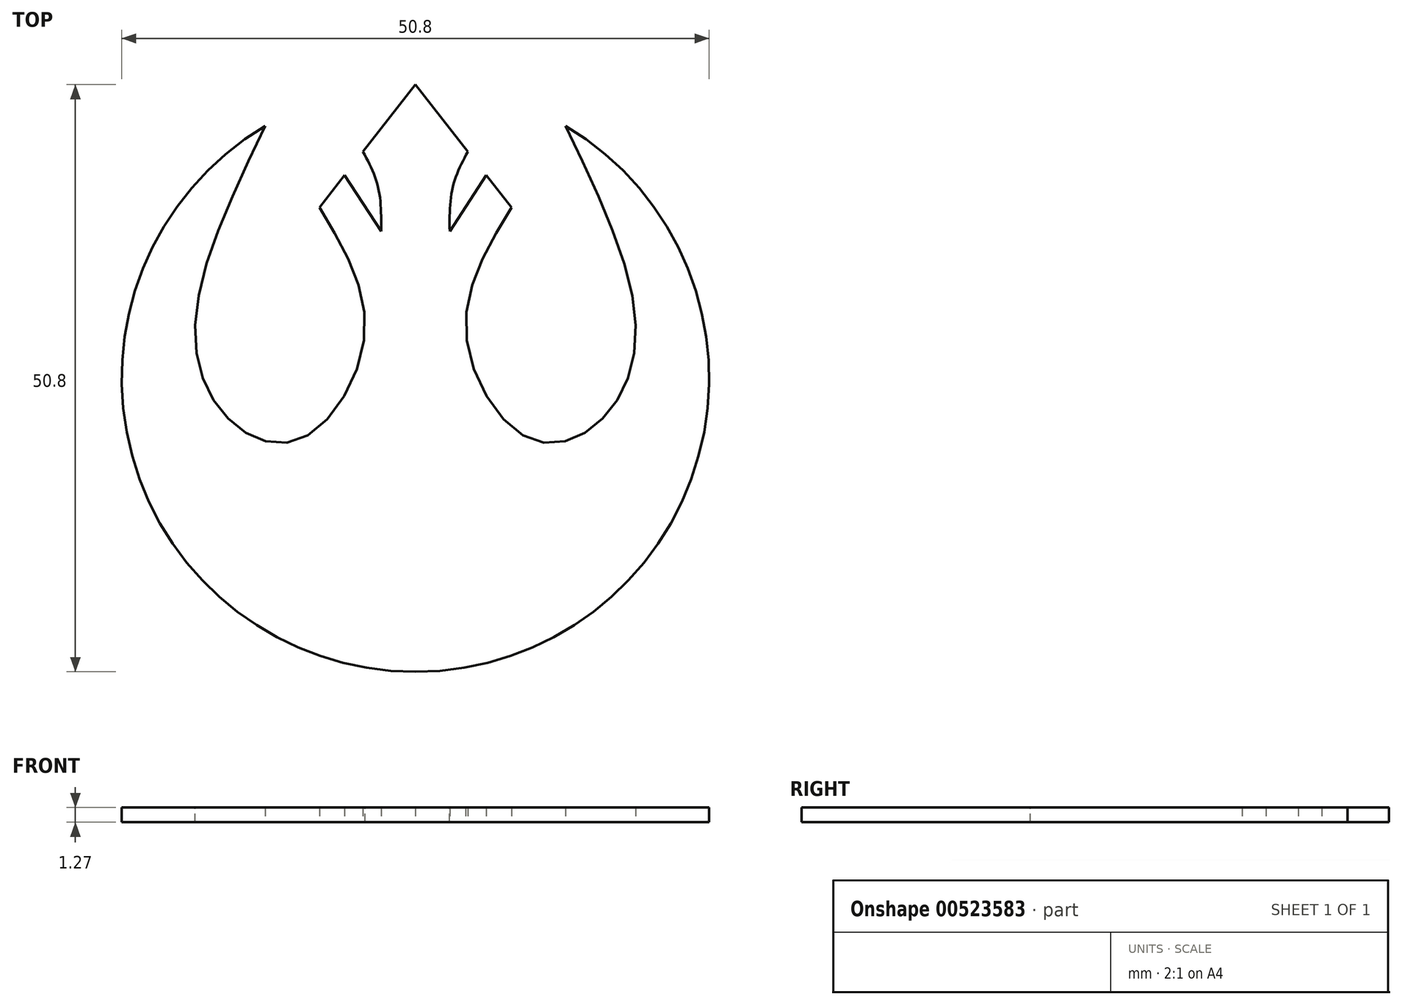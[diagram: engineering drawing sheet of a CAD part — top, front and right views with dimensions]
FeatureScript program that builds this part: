
annotation { "Feature Type Name" : "Feature", "Feature Type Description" : "" }
export const myFeature = defineFeature(function(context is Context, id is Id, definition is map)
    precondition{}
    {
        {
            var Q0;
            Q0=qCreatedBy(makeId("Top.planeOp"),FACE);
            var sketch = newSketch(context, id + "F0", { "sketchPlane" : qUnion([Q0])});
            skArc(sketch, "E0", {"start": v(-36.16, 53.46) * mm, "mid": v(-61.56, 28.06) * mm, "end": v(-36.16, 2.66) * mm});
            skLineSegment(sketch, "E1", {"start": v(-36.16, 53.46) * mm, "end": v(-36.16, 2.66) * mm});
            skLineSegment(sketch, "E2", {"start": v(-44.46, 42.82) * mm, "end": v(-36.16, 53.46) * mm});
            skLineSegment(sketch, "E3", {"start": v(-42.28, 45.62) * mm, "end": v(-39.13, 40.76) * mm});
            skFitSpline(sketch, "E4", {"points": [v(-40.69, 47.66) * mm, v(-39.38, 44.57) * mm, v(-39.13, 40.76) * mm], "startDerivative": vector(3.24, -6.13) * mm, "endDerivative": vector(-0.1, -7.65) * mm});
            skFitSpline(sketch, "E5", {"points": [v(-49.14, 49.89) * mm, v(-55.21, 32.66) * mm, v(-52.14, 24.37) * mm, v(-46.1, 22.8) * mm, v(-40.53, 31.92) * mm, v(-44.46, 42.82) * mm], "startDerivative": vector(-33.92, -70.48) * mm, "endDerivative": vector(-30.58, 50.45) * mm});
            skSolve(sketch);
        }
        {
            var Q0;
            {var subQ1=sQuery(id+"F0.wireOp",EDGE,"E1");Q0=makeQuery(id+"F0.imprint","IMPRINT",FACE,{"disambiguationData":[TD([[makeQuery(id+"F0.imprint","IMPRINT",EDGE,{"derivedFrom":subQ1}),-1.0]])]});}
            extrude(context, id + "F1", {"entities" : qUnion([Q0]), "offsetDistance" : 25.4 * mm, "depth" : 1.27 * mm});
        }
        {
            var Q0;
            Q0=makeQuery(id+"F1.opExtrude","SWEPT_BODY",BODY,{"disambiguationData":[OSD([sQuery(id+"F0.wireOp",EDGE,"E0"),sQuery(id+"F0.wireOp",EDGE,"E1"),sQuery(id+"F0.wireOp",EDGE,"E2"),sQuery(id+"F0.wireOp",EDGE,"E3"),sQuery(id+"F0.wireOp",EDGE,"E4"),sQuery(id+"F0.wireOp",EDGE,"E5")])]});
            var Q1;
            Q1=makeQuery(id+"F1.opExtrude","SWEPT_FACE",FACE,{"disambiguationData":[OSD([sQuery(id+"F0.wireOp",EDGE,"E1")])]});
            mirror(context, id + "F2", {"operationType" : NewBodyOperationType.ADD, "entities" : qUnion([Q0]), "mirrorPlane" : qUnion([Q1])});
        }
    });
